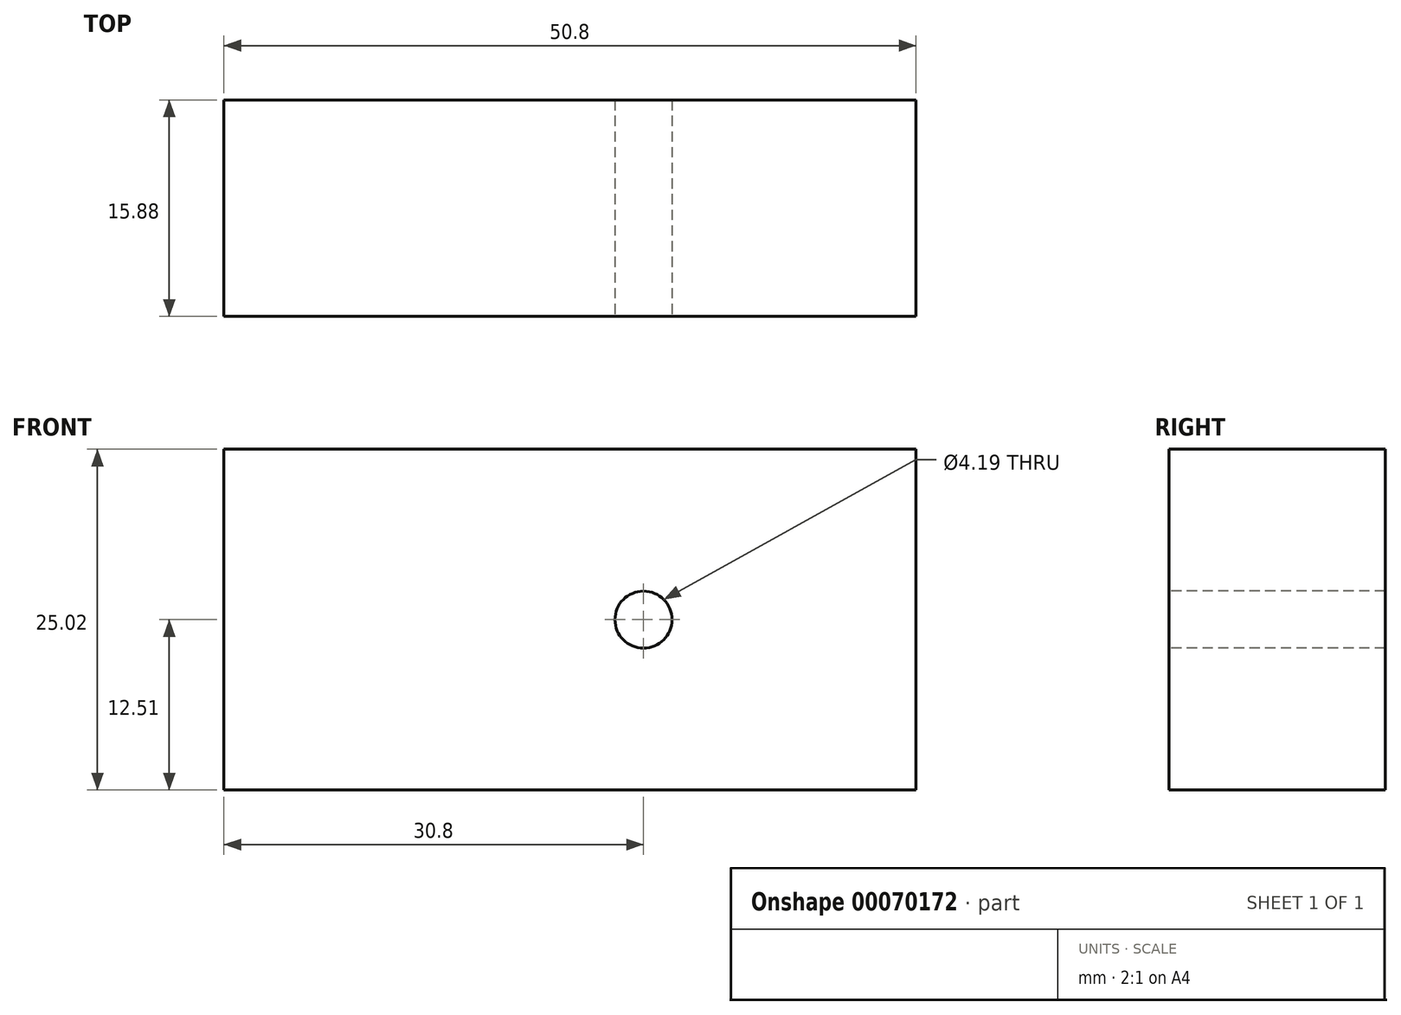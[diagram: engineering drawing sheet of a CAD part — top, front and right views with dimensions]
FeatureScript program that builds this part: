
annotation { "Feature Type Name" : "Feature", "Feature Type Description" : "" }
export const myFeature = defineFeature(function(context is Context, id is Id, definition is map)
    precondition{}
    {
        {
            var Q0;
            Q0=qCreatedBy(makeId("Front.planeOp"),FACE);
            var sketch = newSketch(context, id + "F0", { "sketchPlane" : qUnion([Q0])});
            skLineSegment(sketch, "E0.rect.bottom", {"start": v(-25.4, -12.5) * mm, "end": v(25.4, -12.5) * mm});
            skLineSegment(sketch, "E0.rect.top", {"start": v(-25.4, 12.5) * mm, "end": v(25.4, 12.5) * mm});
            skLineSegment(sketch, "E0.rect.left", {"start": v(-25.4, -12.5) * mm, "end": v(-25.4, 12.5) * mm});
            skLineSegment(sketch, "E0.rect.right", {"start": v(25.4, -12.5) * mm, "end": v(25.4, 12.5) * mm});
            skPoint(sketch, "E0.rect.middle", {"position": v(0, 0) * mm});
            skSolve(sketch);
        }
        {
            var Q0;
            Q0 = qSketchRegion(id + "F0", true);
            extrude(context, id + "F1", {"entities" : qUnion([Q0]), "depth" : 15.88 * mm});
        }
        {
            var Q0;
            Q0=makeQuery(id+"F1.opExtrude","CAP_FACE",FACE,{"disambiguationData":[OSD([sQuery(id+"F0.wireOp",EDGE,"E0.rect.bottom"),sQuery(id+"F0.wireOp",EDGE,"E0.rect.top"),sQuery(id+"F0.wireOp",EDGE,"E0.rect.left"),sQuery(id+"F0.wireOp",EDGE,"E0.rect.right")])],"isStart":false});
            var sketch = newSketch(context, id + "F2", { "sketchPlane" : qUnion([Q0])});
            skPoint(sketch, "E1", {"position": v(5.4, 0) * mm});
            skSolve(sketch);
        }
        {
            var Q0;
            Q0=sQuery(id+"F2.wireOp",VERTEX,"E1");
            var Q1;
            Q1=makeQuery(id+"F1.opExtrude","SWEPT_BODY",BODY,{"disambiguationData":[OSD([sQuery(id+"F0.wireOp",EDGE,"E0.rect.bottom"),sQuery(id+"F0.wireOp",EDGE,"E0.rect.top"),sQuery(id+"F0.wireOp",EDGE,"E0.rect.left"),sQuery(id+"F0.wireOp",EDGE,"E0.rect.right")])]});
            hole(context, id + "F3", {"style" : HoleStyle.SIMPLE, "holeDiameter" : 4.2 * mm, "endStyle" : HoleEndStyle.THROUGH, "locations" : qUnion([Q0]), "scope" : qUnion([Q1])});
        }
    });
